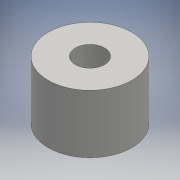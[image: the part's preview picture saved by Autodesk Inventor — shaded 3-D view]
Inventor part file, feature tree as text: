
AUTODESK INVENTOR PART (.ipt)
format: ipt  version: 2016 (Build 200138000, 138)  size: 87,552 bytes
history: native  units: mm
features: extrude x1, sketch x1
ambient origin geometry x8: Origin, YZ Plane, XZ Plane, XY Plane, X Axis, Y Axis, Z Axis, Center Point
bodies: Solid1 (feature_tree)
feature tree (2):
  extrude  "Extrusion1"  Depth=10.0mm
  sketch  "Sketch1"  dims[d0=3.5mm d1=10.0mm d2=7.0mm d3=0.0mm]
